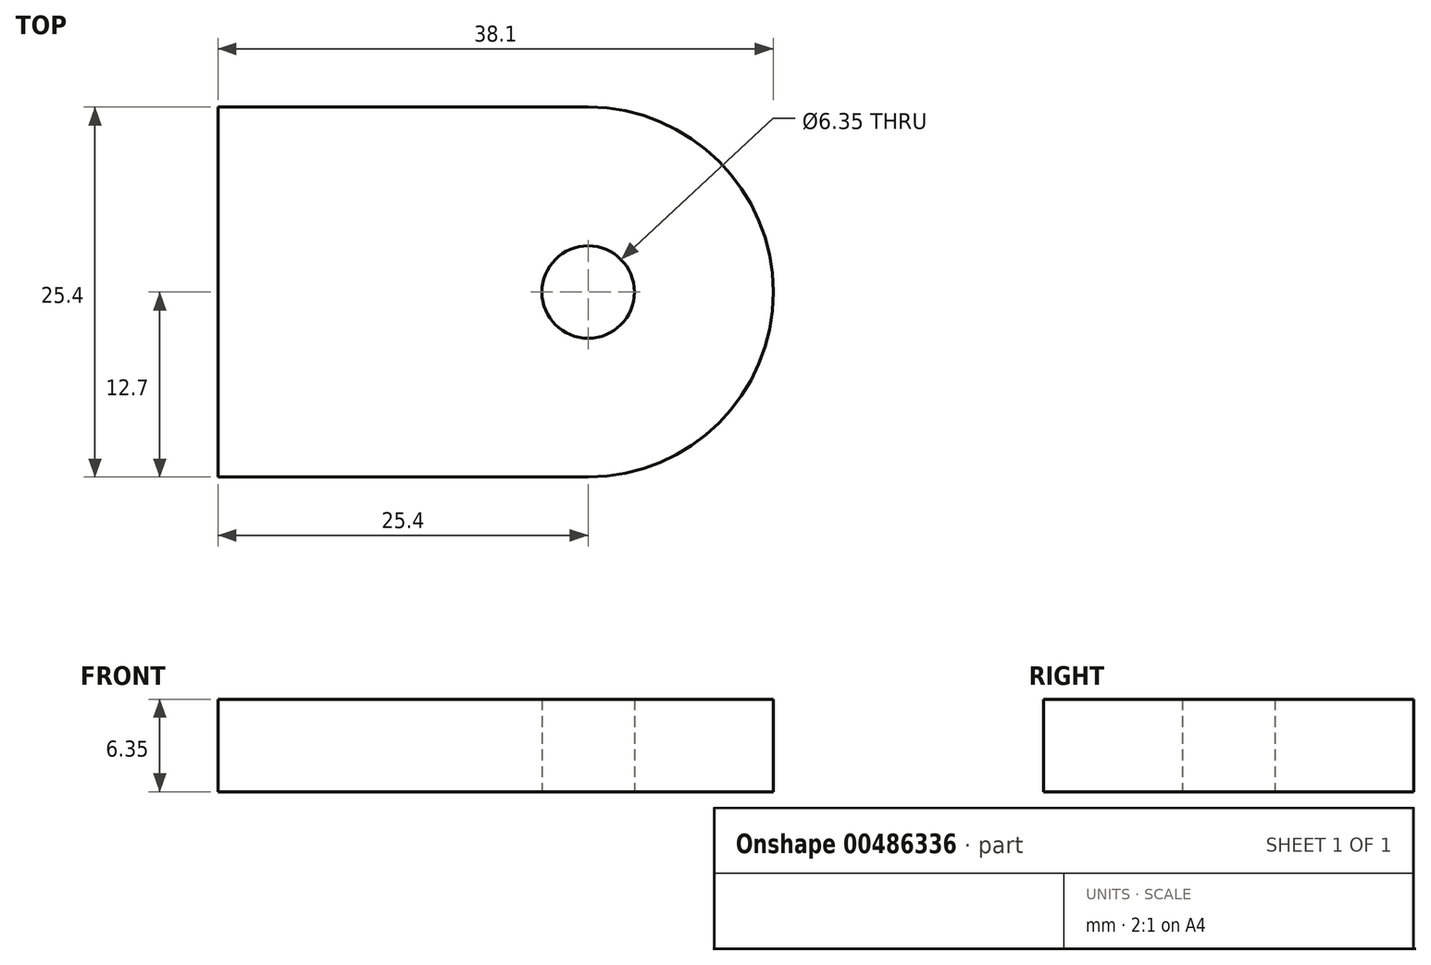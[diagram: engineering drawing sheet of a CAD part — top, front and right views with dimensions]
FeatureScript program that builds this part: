
annotation { "Feature Type Name" : "Feature", "Feature Type Description" : "" }
export const myFeature = defineFeature(function(context is Context, id is Id, definition is map)
    precondition{}
    {
        {
            var Q0;
            Q0=qCreatedBy(makeId("Top.planeOp"),FACE);
            var sketch = newSketch(context, id + "F0", { "sketchPlane" : qUnion([Q0])});
            skLineSegment(sketch, "E0.bottom", {"start": v(-12.7, -12.7) * mm, "end": v(12.7, -12.7) * mm});
            skLineSegment(sketch, "E0.top", {"start": v(-12.7, 12.7) * mm, "end": v(12.7, 12.7) * mm});
            skLineSegment(sketch, "E0.left", {"start": v(-12.7, -12.7) * mm, "end": v(-12.7, 12.7) * mm});
            skLineSegment(sketch, "E0.right", {"start": v(12.7, -12.7) * mm, "end": v(12.7, 12.7) * mm});
            skPoint(sketch, "E0.middle", {"position": v(0, 0) * mm});
            skArc(sketch, "E1", {"start": v(12.7, -12.7) * mm, "mid": v(25.4, 0) * mm, "end": v(12.7, 12.7) * mm});
            skCircle(sketch, "E2", {"center": v(12.7, 0) * mm, "radius": 3.18 * mm});
            skSolve(sketch);
        }
        {
            var Q0;
            Q0 = qSketchRegion(id + "F0", true);
            extrude(context, id + "F1", {"entities" : qUnion([Q0]), "depth" : 6.35 * mm});
        }
    });
